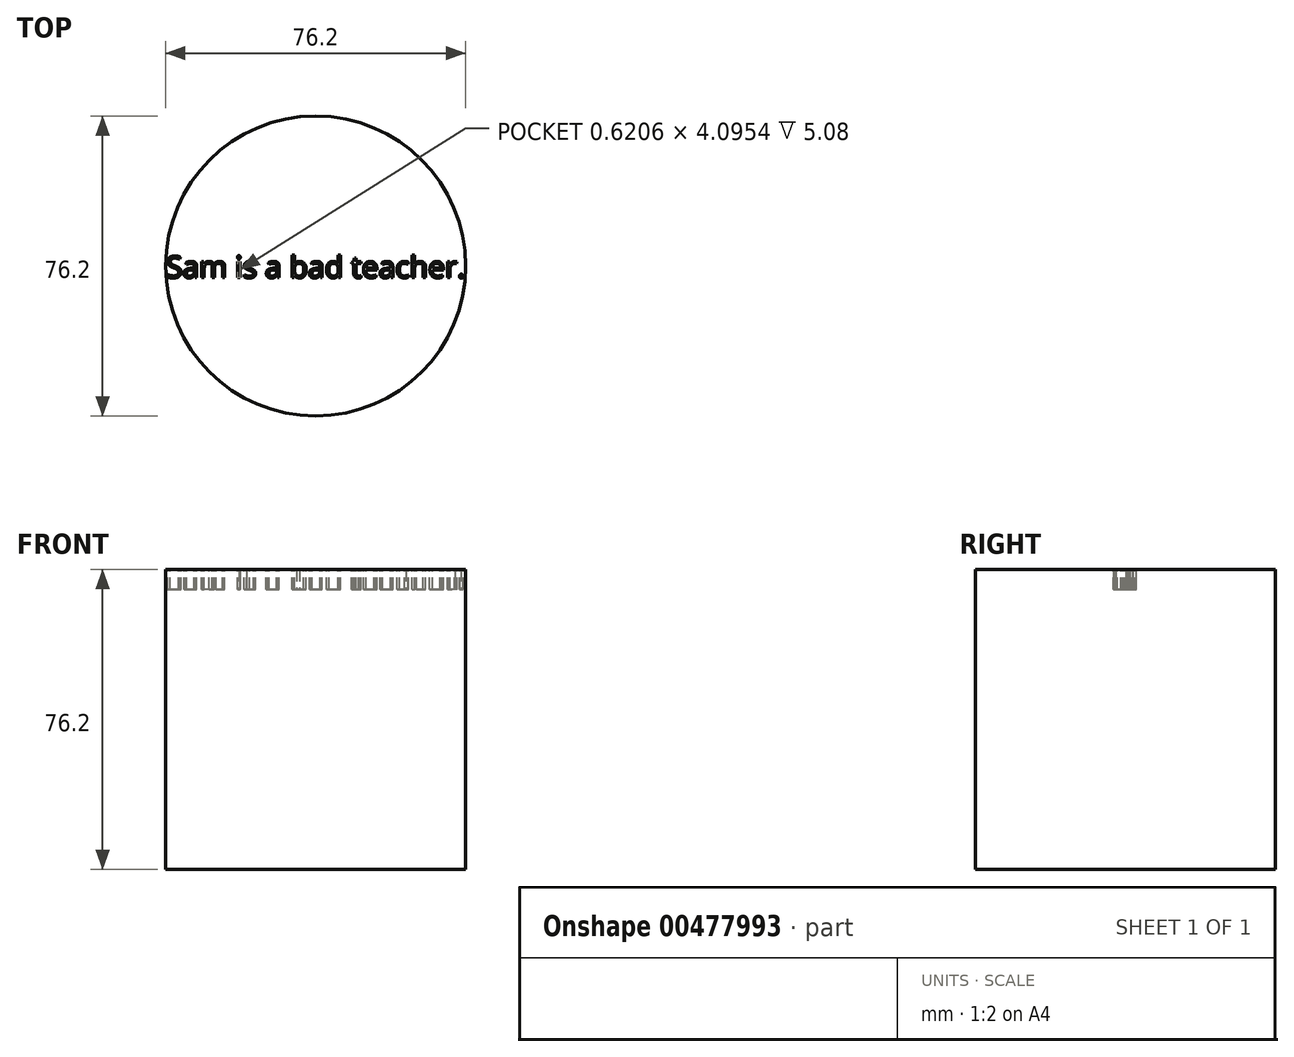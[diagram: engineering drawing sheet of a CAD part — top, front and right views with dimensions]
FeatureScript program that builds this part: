
annotation { "Feature Type Name" : "Feature", "Feature Type Description" : "" }
export const myFeature = defineFeature(function(context is Context, id is Id, definition is map)
    precondition{}
    {
        {
            var Q0;
            Q0=qCreatedBy(makeId("Top.planeOp"),FACE);
            var sketch = newSketch(context, id + "F0", { "sketchPlane" : qUnion([Q0])});
            skCircle(sketch, "E0", {"center": v(0, 0) * mm, "radius": 38.1 * mm});
            skSolve(sketch);
        }
        {
            var Q0;
            Q0 = qSketchRegion(id + "F0", true);
            extrude(context, id + "F1", {"entities" : qUnion([Q0]), "depth" : 76.2 * mm});
        }
        {
            var Q0;
            Q0=makeQuery(id+"F1.opExtrude","CAP_FACE",FACE,{"disambiguationData":[OSD([sQuery(id+"F0.wireOp",EDGE,"E0")])],"isStart":false});
            var sketch = newSketch(context, id + "F2", { "sketchPlane" : qUnion([Q0])});
            skText(sketch, "E1", { "text": "Sam is a bad teacher.", "fontName": "OpenSans-Regular.ttf"});
            const initialGuessF2  = {"E1": [-0.03802, -0.00297, 1, 0, 0.00551]};
            skSetInitialGuess(sketch, initialGuessF2);
            skSolve(sketch);
        }
        {
            var Q0;
            Q0 = qSketchRegion(id + "F2", true);
            extrude(context, id + "F3", {"entities" : qUnion([Q0]), "operationType" : NewBodyOperationType.REMOVE, "oppositeDirection" : true, "depth" : 5.08 * mm});
        }
    });
